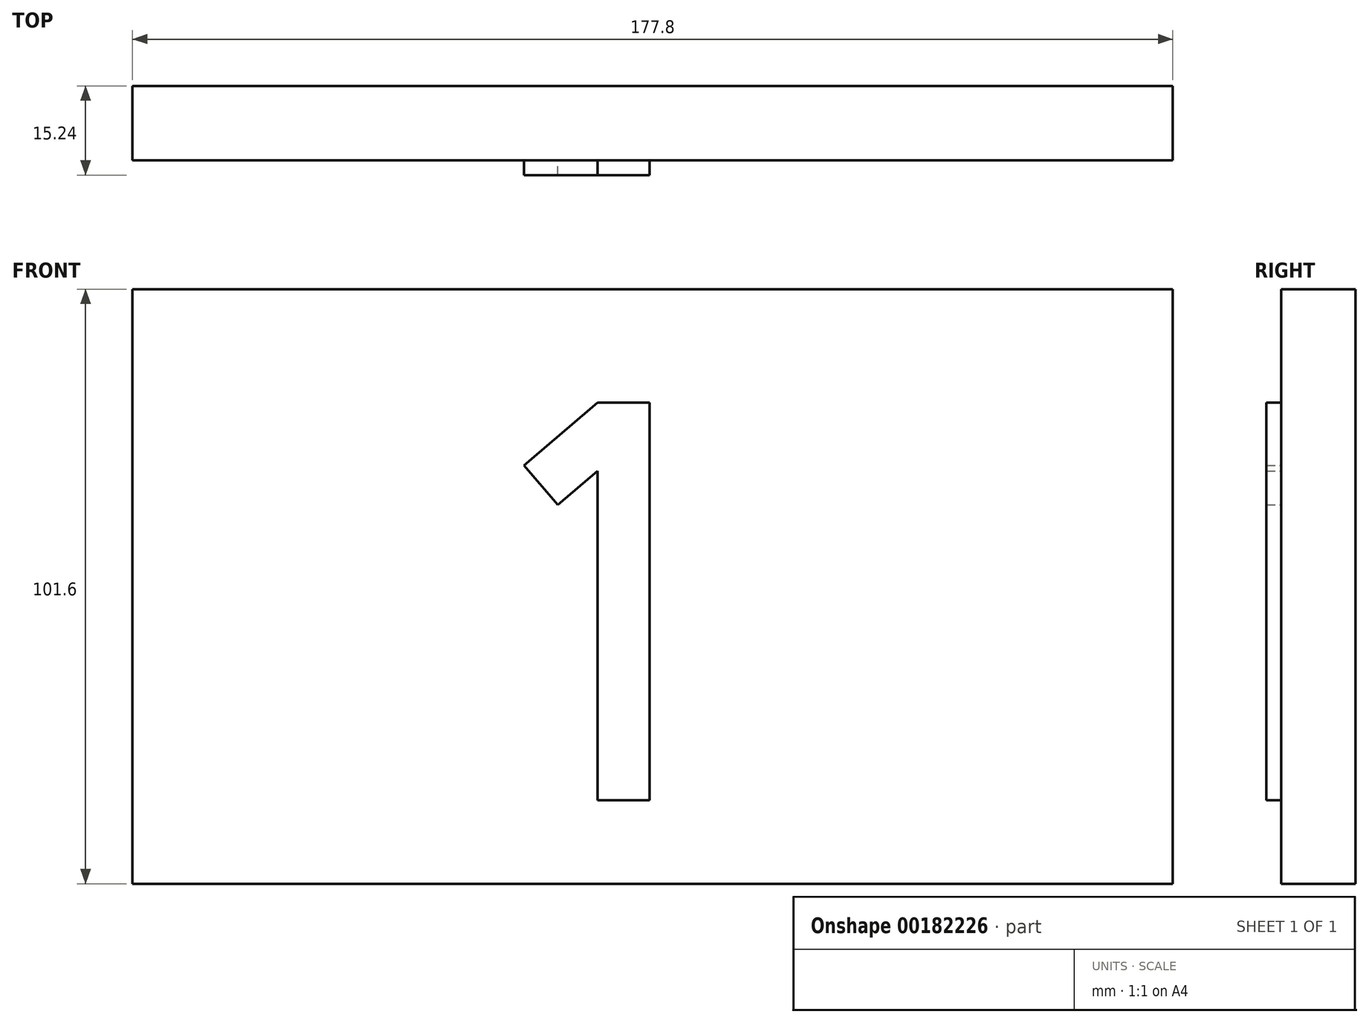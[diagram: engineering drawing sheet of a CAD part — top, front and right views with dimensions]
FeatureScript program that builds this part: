
annotation { "Feature Type Name" : "Feature", "Feature Type Description" : "" }
export const myFeature = defineFeature(function(context is Context, id is Id, definition is map)
    precondition{}
    {
        {
            var Q0;
            Q0=qCreatedBy(makeId("Front.planeOp"),FACE);
            var sketch = newSketch(context, id + "F0", { "sketchPlane" : qUnion([Q0])});
            skLineSegment(sketch, "E0.bottom", {"start": v(0, 0) * mm, "end": v(177.8, 0) * mm});
            skLineSegment(sketch, "E0.top", {"start": v(0, 101.6) * mm, "end": v(177.8, 101.6) * mm});
            skLineSegment(sketch, "E0.left", {"start": v(0, 0) * mm, "end": v(0, 101.6) * mm});
            skLineSegment(sketch, "E0.right", {"start": v(177.8, 0) * mm, "end": v(177.8, 101.6) * mm});
            skSolve(sketch);
        }
        {
            var Q0;
            Q0=makeQuery(id+"F0.imprint","IMPRINT",FACE,{"disambiguationData":[TD([[makeQuery(id+"F0.imprint","IMPRINT",EDGE,{"derivedFrom":sQuery(id+"F0.wireOp",EDGE,"E0.bottom")}),1.0]])]});
            extrude(context, id + "F1", {"entities" : qUnion([Q0]), "oppositeDirection" : true, "depth" : 12.7 * mm});
        }
        {
            var Q0;
            Q0=makeQuery(id+"F1.opExtrude","CAP_FACE",FACE,{"disambiguationData":[OSD([sQuery(id+"F0.wireOp",EDGE,"E0.bottom"),sQuery(id+"F0.wireOp",EDGE,"E0.top"),sQuery(id+"F0.wireOp",EDGE,"E0.left"),sQuery(id+"F0.wireOp",EDGE,"E0.right")])],"isStart":true});
            var sketch = newSketch(context, id + "F2", { "sketchPlane" : qUnion([Q0])});
            skLineSegment(sketch, "E1.bottom", {"start": v(79.46, 82.2) * mm, "end": v(88.35, 82.2) * mm});
            skLineSegment(sketch, "E1.top", {"start": v(79.46, 14.28) * mm, "end": v(88.35, 14.28) * mm});
            skLineSegment(sketch, "E1.left", {"start": v(79.46, 70.5) * mm, "end": v(79.46, 14.28) * mm});
            skLineSegment(sketch, "E1.right", {"start": v(88.35, 82.2) * mm, "end": v(88.35, 14.28) * mm});
            skLineSegment(sketch, "E2", {"start": v(79.46, 82.2) * mm, "end": v(66.93, 71.48) * mm});
            skLineSegment(sketch, "E3", {"start": v(66.93, 71.48) * mm, "end": v(72.7, 64.72) * mm});
            skLineSegment(sketch, "E4", {"start": v(72.7, 64.72) * mm, "end": v(79.46, 70.5) * mm});
            skSolve(sketch);
        }
        {
            var Q0;
            Q0=qSketchRegion(id+"F2",true);
            extrude(context, id + "F3", {"entities" : qUnion([Q0]), "operationType" : NewBodyOperationType.ADD, "depth" : 2.54 * mm});
        }
    });
